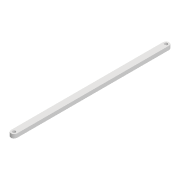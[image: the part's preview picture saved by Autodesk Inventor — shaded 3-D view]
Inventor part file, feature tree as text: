
AUTODESK INVENTOR PART (.ipt)
format: ipt  version: 2022 (Build 260153000, 153)  size: 86,528 bytes
history: native  units: mm
features: extrude x1, sketch x1
ambient origin geometry x8: Origin, YZ Plane, XZ Plane, XY Plane, X Axis, Y Axis, Z Axis, Center Point
bodies: Solid1 (feature_tree)
feature tree (2):
  extrude  "Extrusion1"  Depth=8.0mm
  sketch  "Sketch1"  dims[d0=195.0mm d1=8.0mm d2=4.2mm d3=4.2mm d4=5.0mm d5=0.0mm]
